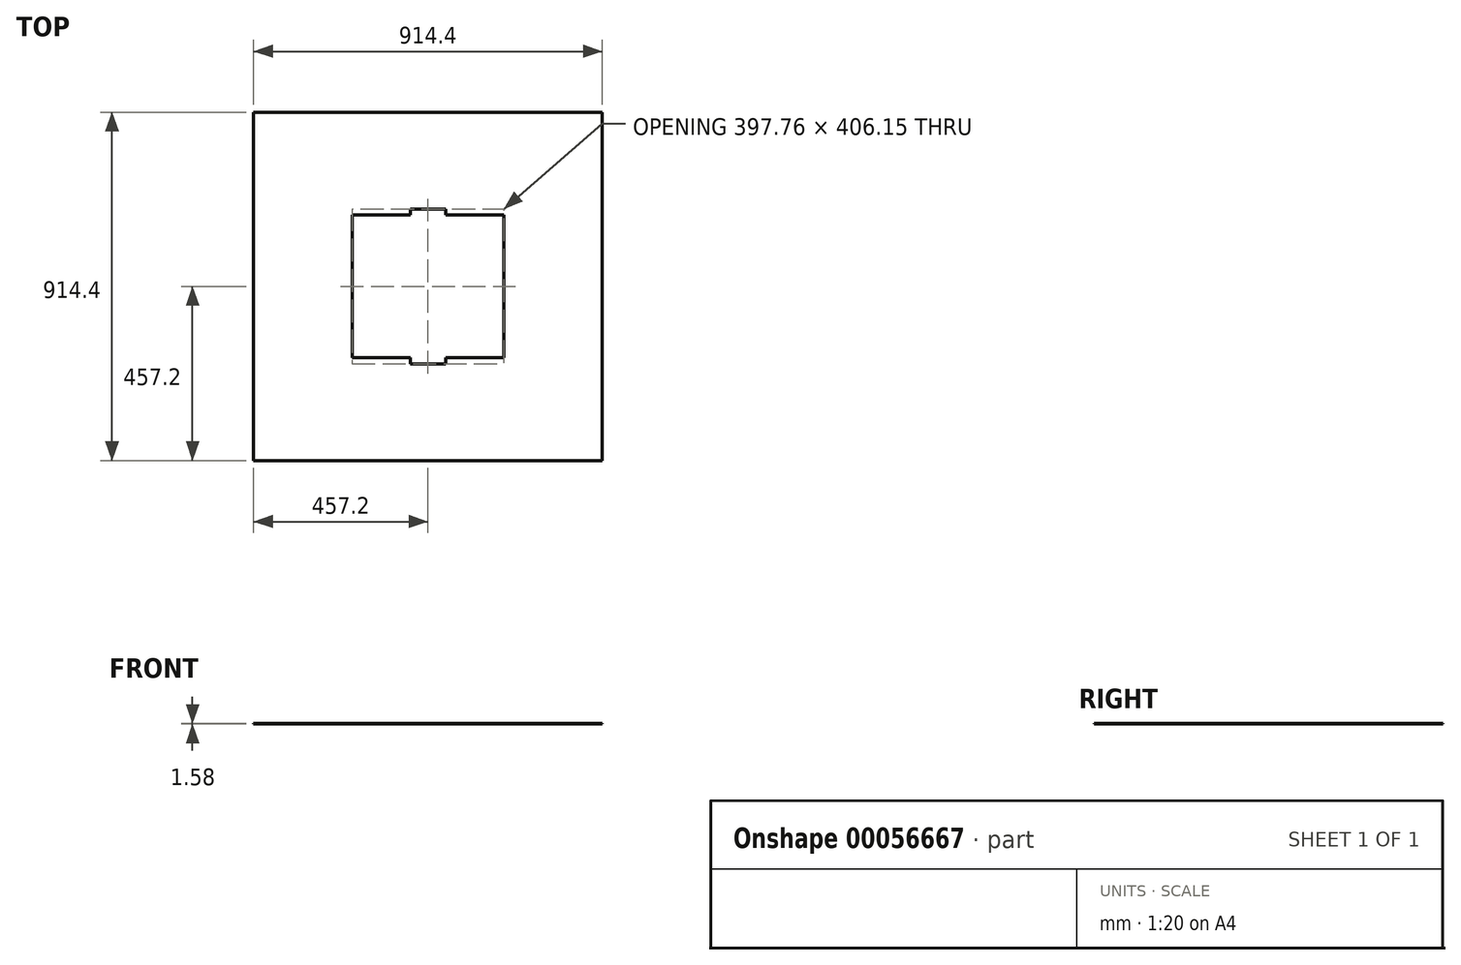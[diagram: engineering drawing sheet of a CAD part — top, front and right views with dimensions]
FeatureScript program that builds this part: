
annotation { "Feature Type Name" : "Feature", "Feature Type Description" : "" }
export const myFeature = defineFeature(function(context is Context, id is Id, definition is map)
    precondition{}
    {
        {
            var Q0;
            Q0=qCreatedBy(makeId("Top.planeOp"),FACE);
            var sketch = newSketch(context, id + "F0", { "sketchPlane" : qUnion([Q0])});
            skLineSegment(sketch, "E0.rect.bottom", {"start": v(198.88, 187.33) * mm, "end": v(45.97, 187.33) * mm});
            skLineSegment(sketch, "E0.rect.top", {"start": v(198.88, -187.33) * mm, "end": v(45.97, -187.33) * mm});
            skLineSegment(sketch, "E0.rect.left", {"start": v(198.88, 187.33) * mm, "end": v(198.88, -187.33) * mm});
            skLineSegment(sketch, "E0.rect.right", {"start": v(-198.88, 187.33) * mm, "end": v(-198.88, -187.33) * mm});
            skPoint(sketch, "E0.rect.middle", {"position": v(0, 0) * mm});
            skLineSegment(sketch, "E1.rect.bottom", {"start": v(457.2, 457.2) * mm, "end": v(-457.2, 457.2) * mm});
            skLineSegment(sketch, "E1.rect.top", {"start": v(457.2, -457.2) * mm, "end": v(-457.2, -457.2) * mm});
            skLineSegment(sketch, "E1.rect.left", {"start": v(457.2, 457.2) * mm, "end": v(457.2, -457.2) * mm});
            skLineSegment(sketch, "E1.rect.right", {"start": v(-457.2, 457.2) * mm, "end": v(-457.2, -457.2) * mm});
            skLineSegment(sketch, "E2", {"start": v(-45.97, 187.32) * mm, "end": v(-45.97, 203.07) * mm});
            skLineSegment(sketch, "E3", {"start": v(-45.97, 203.07) * mm, "end": v(45.97, 203.07) * mm});
            skLineSegment(sketch, "E4", {"start": v(45.97, 203.07) * mm, "end": v(45.97, 187.32) * mm});
            skLineSegment(sketch, "E5", {"start": v(-45.97, -187.33) * mm, "end": v(-45.97, -203.07) * mm});
            skLineSegment(sketch, "E6", {"start": v(-45.97, -203.07) * mm, "end": v(45.97, -203.07) * mm});
            skLineSegment(sketch, "E7", {"start": v(45.97, -203.07) * mm, "end": v(45.97, -187.33) * mm});
            skLineSegment(sketch, "E8.trimOffspring", {"start": v(-45.97, 187.33) * mm, "end": v(-198.88, 187.33) * mm});
            skLineSegment(sketch, "E9.trimOffspring", {"start": v(-45.97, -187.33) * mm, "end": v(-198.88, -187.33) * mm});
            skSolve(sketch);
        }
        {
            var Q0;
            Q0 = qSketchRegion(id + "F0", true);
            extrude(context, id + "F1", {"entities" : qUnion([Q0]), "endBound" : BoundingType.SYMMETRIC, "depth" : 1.59 * mm});
        }
    });
